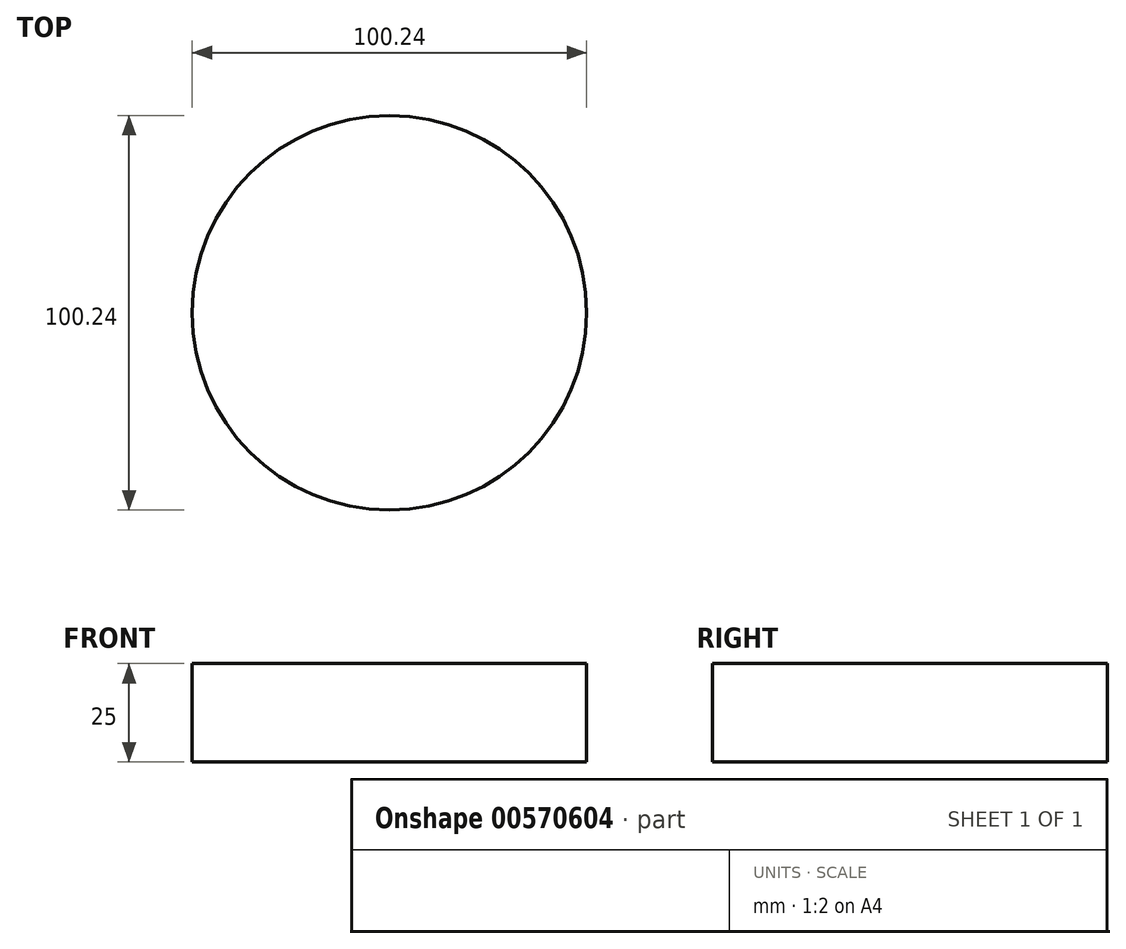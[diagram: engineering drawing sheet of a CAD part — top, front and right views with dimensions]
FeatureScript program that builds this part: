
annotation { "Feature Type Name" : "Feature", "Feature Type Description" : "" }
export const myFeature = defineFeature(function(context is Context, id is Id, definition is map)
    precondition{}
    {
        {
            var Q0;
            Q0=qCreatedBy(makeId("Top.planeOp"),FACE);
            var sketch = newSketch(context, id + "F0", { "sketchPlane" : qUnion([Q0])});
            skCircle(sketch, "E0", {"center": v(0, 0) * mm, "radius": 50.12 * mm});
            skCircle(sketch, "E1", {"center": v(0, 0) * mm, "radius": 30 * mm});
            skSolve(sketch);
        }
        {
            var Q0;
            Q0=makeQuery(id+"F0.imprint","IMPRINT",FACE,{"disambiguationData":[TD([[makeQuery(id+"F0.imprint","IMPRINT",EDGE,{"derivedFrom":sQuery(id+"F0.wireOp",EDGE,"E0")}),1.0]])]});
            var Q1;
            Q1=makeQuery(id+"F0.imprint","IMPRINT",FACE,{"disambiguationData":[TD([[makeQuery(id+"F0.imprint","IMPRINT",EDGE,{"derivedFrom":sQuery(id+"F0.wireOp",EDGE,"E1")}),1.0]])]});
            extrude(context, id + "F1", {"entities" : qUnion([Q0, Q1]), "depth" : 25 * mm, "offsetDistance" : 25 * mm});
        }
    });
